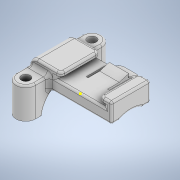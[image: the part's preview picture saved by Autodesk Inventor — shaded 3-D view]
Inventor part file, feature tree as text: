
AUTODESK INVENTOR PART (.ipt)
format: ipt  version: 2020.3 (Build 243373000, 373)  size: 626,176 bytes
history: native  units: mm
features: fillet x15, sketch x8, extrude x7, projected_geometry x1
ambient origin geometry x8: Origin, YZ Plane, XZ Plane, XY Plane, X Axis, Y Axis, Z Axis, Center Point
bodies: Volumenkörper1 (feature_tree)
feature tree (31):
  extrude  "Extrusion1"  Depth=24.0mm
  extrude  "Extrusion2"  Depth=2.0mm
  extrude  "Extrusion3"  Depth=2.0mm
  fillet  "Rundung1"  Radius=20.0mm
  fillet  "Rundung3"  Radius=44.0mm
  fillet  "Rundung4"  Radius=15.8mm
  fillet  "Rundung5"  Radius=26.8mm
  fillet  "Rundung6"  Radius=18.0mm
  extrude  "Extrusion4"  Depth=15.8mm
  extrude  "Extrusion5"  Depth=10.0mm
  sketch  "Skizze6"  dims[d19=4.5mm d20=5.0mm d21=5.0mm d22=5.0mm d23=5.0mm d24=0.0mm d25=0.0mm]
  extrude  "Extrusion6"  Depth=5.0mm
  fillet  "Rundung10"  Radius=5.0mm
  fillet  "Rundung11"  Radius=5.0mm
  fillet  "Rundung12"  Radius=5.0mm
  fillet  "Rundung13"  [1 undecoded]
  extrude  "Extrusion9"  Depth=10.0mm
  fillet  "Rundung15"  Radius=4.0mm
  fillet  "Rundung16"  Radius=1.0mm
  fillet  "Rundung18"  Radius=2.0mm
  fillet  "Rundung19"  Radius=1.0mm
  fillet  "Rundung20"  Radius=10.0mm
  fillet  "Rundung21"  Radius=1.0mm
  sketch  "Skizze1"  dims[d0=20.0mm d2=24.0mm]
  sketch  "Skizze2"  dims[d3=32.0mm d4=2.0mm]
  sketch  "Skizze3"  dims[d5=2.0mm d6=2.0mm d7=20.0mm d8=0.0mm d9=44.0mm d10=15.8mm d11=26.8mm d12=18.0mm]
  sketch  "Skizze4"  dims[d14=22.0mm d15=15.8mm]
  sketch  "Skizze5"  dims[d16=10.0mm d17=0.0mm d18=4.5mm]
  sketch  "Skizze7"  dims[d26=16.0mm d27=5.0mm d29=4.0mm d30=1.0mm d31=2.0mm d32=1.0mm d33=10.0mm d34=1.0mm]
  sketch  "Skizze11"  dims[d35=1.0mm d36=13.129033mm d37=11.0mm d38=5.0mm d39=10.0mm d40=0.0mm d41=1.5mm d42=5.0mm d43=2.0mm d44=4.363323mm d45=7.0mm d46=10.0mm d47=0.0mm d48=1.5mm d49=0.0mm d65=1.0mm d66=1.0mm d67=2.0mm d68=0.5mm d73=10.0mm d74=0.0mm d75=10.0mm d76=20.0mm d77=6.0mm d78=1.0mm d79=1.0mm d81=1.0mm d82=0.9mm d83=2.0mm d84=0.1mm d85=0.19mm d86=0.872665mm d87=0.5mm d88=0.872665mm]
  projected_geometry  "Projizierte Kontur1"
note: 1 required parameter value undecoded (feature->parameter linkage not recoverable at this tier; creation-order binding heuristic only, values carry confidence <= 0.55)
